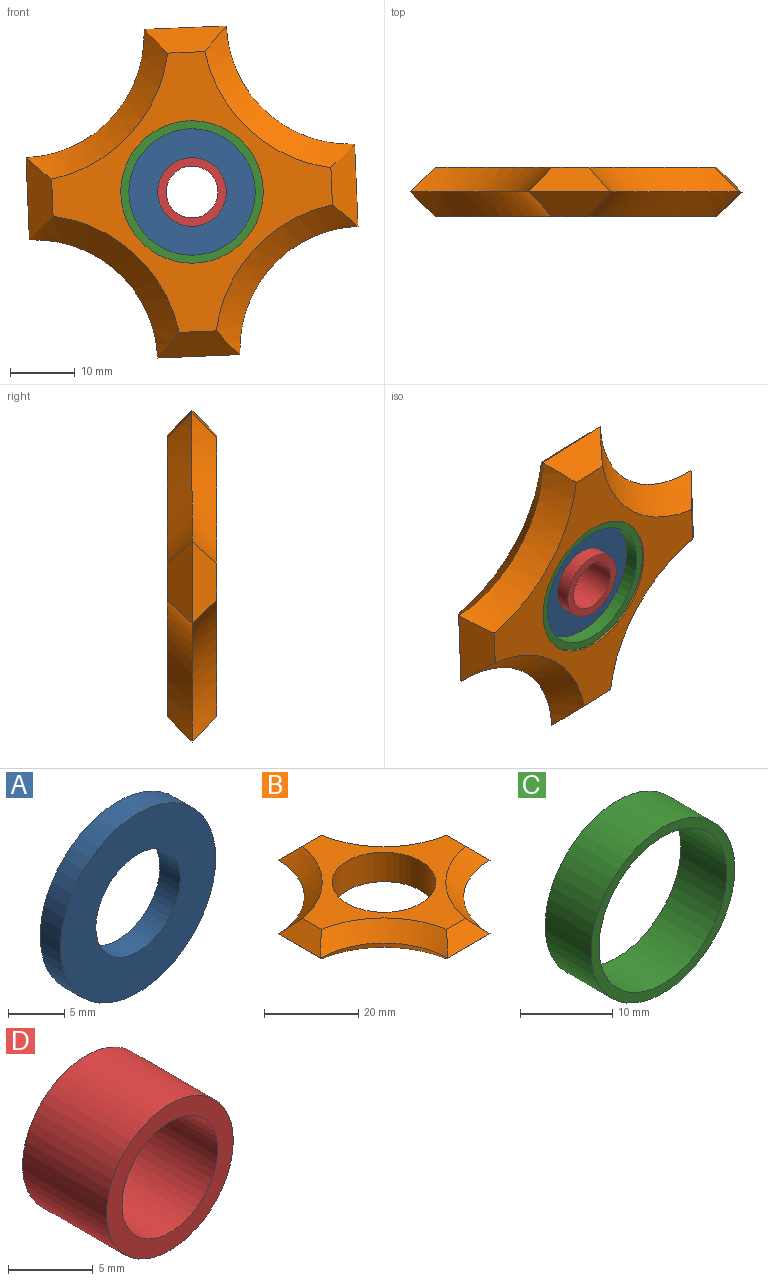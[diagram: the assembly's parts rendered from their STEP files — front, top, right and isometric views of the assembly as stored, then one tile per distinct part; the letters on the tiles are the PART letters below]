
ASSEMBLY  parts=4 mates=3
PART A: 4 faces, bbox 19.5x2.5x19.5 mm
  f0: cylinder r=5.3mm len=10.6mm, axis (0,1,0), area 84.6mm2, adj f2,f3
  f1: cylinder r=9.76mm len=19.52mm, axis (0,1,0), area 155.7mm2, adj f2,f3
  f2: plane 19.52x19.52mm, normal (0,-1,0), area 211mm2, adj f0,f1
  f3: plane 19.52x19.52mm, normal (0,1,0), area 211mm2, adj f0,f1
PART B: 19 faces, bbox 50.8x50.8x7.6 mm
  f0: cylinder r=11mm len=22mm, axis (0,0,-1), area 526.7mm2, adj f1,f2
  f1: plane 43.18x43.18mm, normal (0,0,1), area 478.1mm2, adj f0,f3,f4,f5,f8,f9,f12,f13
  f2: plane 43.18x43.18mm, normal (0,0,-1), area 478.1mm2, adj f0,f6,f7,f10,f11,f14,f15,f17
  f3: plane 12.7x3.81mm, normal (0.71,0,0.71), area 49.1mm2, adj f1,f4,f5,f6
  f4: cone r=19.05mm half-angle=45deg, axis (0,0,1), area 156.8mm2, adj f1,f3,f7,f8
  f5: cone r=19.05mm half-angle=45deg, axis (0,0,1), area 156.8mm2, adj f1,f3,f9,f10
  f6: plane 12.7x3.81mm, normal (0.71,0,-0.71), area 49.1mm2, adj f2,f3,f7,f10
  f7: cone r=22.86mm half-angle=45deg, axis (0,0,-1), area 156.8mm2, adj f2,f4,f6,f11
  f8: plane 12.7x3.81mm, normal (0,0.71,0.71), area 49.1mm2, adj f1,f4,f11,f12
  f9: plane 12.7x3.81mm, normal (0,-0.71,0.71), area 49.1mm2, adj f1,f5,f13,f14
  f10: cone r=22.86mm half-angle=45deg, axis (0,0,-1), area 156.8mm2, adj f2,f5,f6,f14
  f11: plane 12.7x3.81mm, normal (0,0.71,-0.71), area 49.1mm2, adj f2,f7,f8,f15
  f12: cone r=22.86mm half-angle=45deg, axis (0,0,1), area 156.8mm2, adj f1,f8,f15,f16
  f13: cone r=22.86mm half-angle=45deg, axis (0,0,1), area 156.8mm2, adj f1,f9,f16,f17
  f14: plane 12.7x3.81mm, normal (0,-0.71,-0.71), area 49.1mm2, adj f2,f9,f10,f17
  f15: cone r=19.05mm half-angle=45deg, axis (0,0,-1), area 156.8mm2, adj f2,f11,f12,f18
  f16: plane 12.7x3.81mm, normal (-0.71,0,0.71), area 49.1mm2, adj f1,f12,f13,f18
  f17: cone r=19.05mm half-angle=45deg, axis (0,0,-1), area 156.8mm2, adj f2,f13,f14,f18
  f18: plane 12.7x3.81mm, normal (-0.71,0,-0.71), area 49.1mm2, adj f2,f15,f16,f17
PART C: 4 faces, bbox 22x7x22 mm
  f0: cylinder r=9.76mm len=19.52mm, axis (0,1,0), area 429.2mm2, adj f2,f3
  f1: cylinder r=11mm len=22mm, axis (0,1,0), area 483.8mm2, adj f2,f3
  f2: plane 22x22mm, normal (0,-1,0), area 80.9mm2, adj f0,f1
  f3: plane 22x22mm, normal (0,1,0), area 80.9mm2, adj f0,f1
PART D: 4 faces, bbox 10.6x7x10.6 mm
  f0: cylinder r=4mm len=8mm, axis (0,1,0), area 175.9mm2, adj f2,f3
  f1: cylinder r=5.3mm len=10.6mm, axis (0,1,0), area 233.1mm2, adj f2,f3
  f2: plane 10.6x10.6mm, normal (0,-1,0), area 37.9mm2, adj f0,f1
  f3: plane 10.6x10.6mm, normal (0,1,0), area 37.9mm2, adj f0,f1
PLACE A rot(axis=(0,-1,0),2.4deg) t=(9.52,-10.57,-7.45)mm
PLACE B rot(axis=(-1,-0.02,-0.02),90deg) t=(9.52,-14.38,-7.45)mm
PLACE C rot(axis=(0,-1,0),2.4deg) t=(9.52,-10.57,-7.45)mm
PLACE D rot(axis=(0,-1,0),2.4deg) t=(9.52,-10.57,-7.45)mm
MATE fastened A.f0 <-> C.f0  axis (0,1,0) through (9.52,-10.57,-7.45)mm
MATE fastened D.f0 <-> A.f0  axis (0,1,0) through (9.52,-10.57,-7.45)mm
MATE revolute B.f0 <-> C.f0  axis (0,-1,0) through (9.52,-10.57,-7.45)mm
